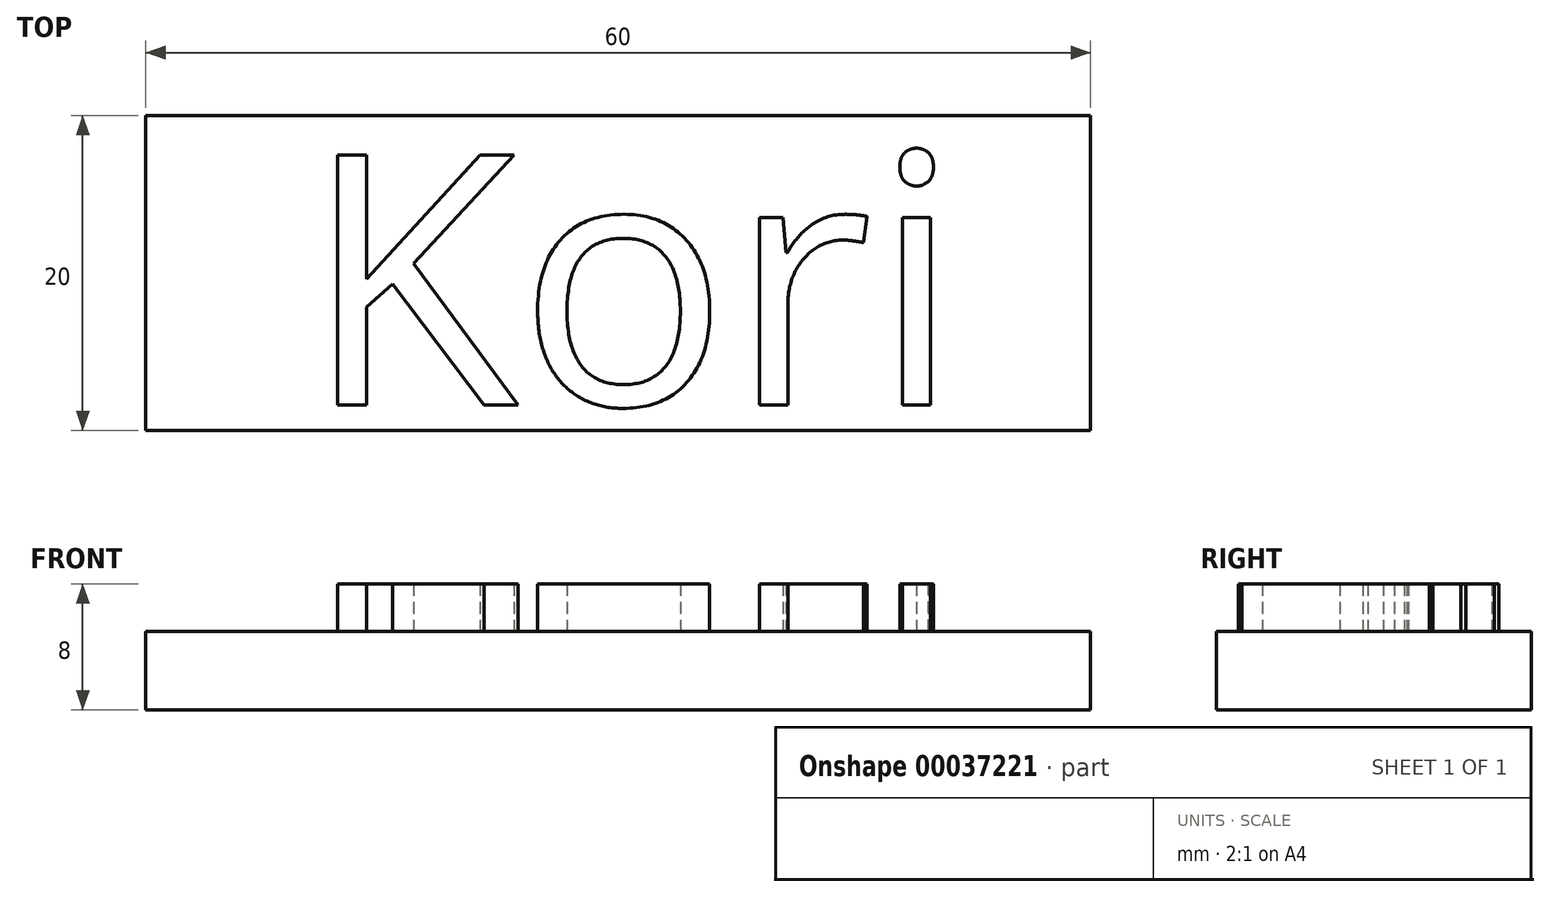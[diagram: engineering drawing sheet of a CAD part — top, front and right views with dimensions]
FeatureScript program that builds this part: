
annotation { "Feature Type Name" : "Feature", "Feature Type Description" : "" }
export const myFeature = defineFeature(function(context is Context, id is Id, definition is map)
    precondition{}
    {
        {
            var Q0;
            Q0=qCreatedBy(makeId("Top.planeOp"),FACE);
            var sketch = newSketch(context, id + "F0", { "sketchPlane" : qUnion([Q0])});
            skLineSegment(sketch, "E0.rect.bottom", {"start": v(30, 10) * mm, "end": v(-30, 10) * mm});
            skLineSegment(sketch, "E0.rect.top", {"start": v(30, -10) * mm, "end": v(-30, -10) * mm});
            skLineSegment(sketch, "E0.rect.left", {"start": v(30, 10) * mm, "end": v(30, -10) * mm});
            skLineSegment(sketch, "E0.rect.right", {"start": v(-30, 10) * mm, "end": v(-30, -10) * mm});
            skPoint(sketch, "E0.rect.middle", {"position": v(0, 0) * mm});
            skSolve(sketch);
        }
        {
            var Q0;
            Q0 = qSketchRegion(id + "F0", true);
            extrude(context, id + "F1", {"entities" : qUnion([Q0]), "depth" : 5 * mm});
        }
        {
            var Q0;
            Q0=makeQuery(id+"F1.opExtrude","CAP_FACE",FACE,{"disambiguationData":[OSD([sQuery(id+"F0.wireOp",EDGE,"E0.rect.bottom"),sQuery(id+"F0.wireOp",EDGE,"E0.rect.top"),sQuery(id+"F0.wireOp",EDGE,"E0.rect.left"),sQuery(id+"F0.wireOp",EDGE,"E0.rect.right")])],"isStart":false});
            var sketch = newSketch(context, id + "F2", { "sketchPlane" : qUnion([Q0])});
            skText(sketch, "E1", { "text": "Kori", "fontName": "OpenSans-Regular.ttf"});
            const initialGuessF2  = {"E1": [-0.02, -0.00838, 1, 0, 0.016]};
            skSetInitialGuess(sketch, initialGuessF2);
            skSolve(sketch);
        }
        {
            var Q0;
            Q0 = qSketchRegion(id + "F2", true);
            extrude(context, id + "F3", {"entities" : qUnion([Q0]), "operationType" : NewBodyOperationType.ADD, "depth" : 3 * mm});
        }
    });
